# Revit family: Рондо
name_source: partatom
category: Осветительные приборы
units: mm (PartAtom-declared; Revit-internal decimal feet)

## family parameters
Всегда вертикально = Да
Источник света = Да
На основе рабочей плоскости = Нет
Общий = Нет
При загрузке вырезать с полостями = Нет
Размер круглого соединителя = Использовать диаметр
Тип детали = Нормальный
Точка расчета площади = Нет

## types (2) — shared parameters
ADSK_URL страницы изделия = http://www.allfresco.ru
ADSK_Единица измерения = шт.
ADSK_Завод-изготовитель = ALFRESCO
ADSK_Количество фаз = 2
ADSK_Масса = 11
ADSK_Масса_Текст = 11
ADSK_Модель = Рондо ДТУ-79-AF
ADSK_Напряжение = 220 В
ADSK_Полная мощность = 0 В·А
ADSK_Ток = 0 А
ADSK_Энергоэффективность = 110 лм/Вт
D_светильник = 445 мм
D_столб = 102 мм
D_фланец = 240 мм
IP Class = IP 67
d_нижний крепеж = 180 мм
d_светильник = 445 мм
d_шуруп = 378 мм
h_пластина = 5 мм
h_рассеиватель = 5 мм
h_светильник = 105 мм
r светильник = 223 мм
r_УГО = 250 мм
r_отверстия пластина = 3 мм
r_пластина = 120 мм
r_рассеиватель = 218 мм
r_столб = 51 мм
Блок аварийного питания = Нет
Видимая форма излучения при визуализации = Нет
Излучение по диаметру окружности = 445 мм
Класс защиты = 1
Класс пожароопасности = F (светильники предназначены для установки непосредственно на поверхность из нормально воспламеняемых материалов)
Климатическая зона = УХЛ1
Корпус светильника = Серый металл
Материал рассеивателя = Светотехнический ПК
Область использования = Парки, скверы, общественные пространства, городская инфраструктура
Полная установленная мощность = 0 В·А
Рассеиватель = Материал рассеивателя
Светофильтр = 16777215
Смещение цветовой температуры при затухании лампы = <Нет>
Таблица выбора = Таблица параметров светильников
Температура эксплуатации = -40 +50
Тип ИС = LED-модуль
Тип КСС = тип Д (косинусная)
Тип ПРА = -
Тип продукции = LED-светильник
Угол наклона = 90.00°
Цветоывая температура = 2700-5500
zero-valued in all types: ADSK_Количество фаз числовое, ADSK_Коэффициент мощности

## per-type parameters (varying)
| type | ADSK_Артикул | ADSK_Наименование | ADSK_Номинальная мощность | ADSK_Размер_Высота | ADSK_Фактическая мощность | h_столб | Файл фотометрической сетки |
| ДТУ791 Светодиодный светильник Рондо ДТУ-79-AF-25Вт(d76) на опоре ОС 4м | ДТУ791 | ДТУ791 Светодиодный светильник Рондо ДТУ-79-AF-25Вт(d76) на опоре ОС 4м | 25 Вт | 4000 мм | 25 Вт | 4197 мм | DTU-79-AF Rondo 25W.ies |
| ДТУ791 Светодиодный светильник Рондо ДТУ-79-AF-25Вт(d76) на опоре ОС 5м | ДТУ792 | ДТУ792 Светодиодный светильник Рондо ДТУ-79-AF-50Вт(d76) на опоре ОС 5м | 50 Вт | 5000 мм | 50 Вт | 5197 мм | DTU-79-AF Rondo 50 W.ies |

## geometry (parser evidence)
native form markers: Blend x4
no freeform markers — native parametric forms only
